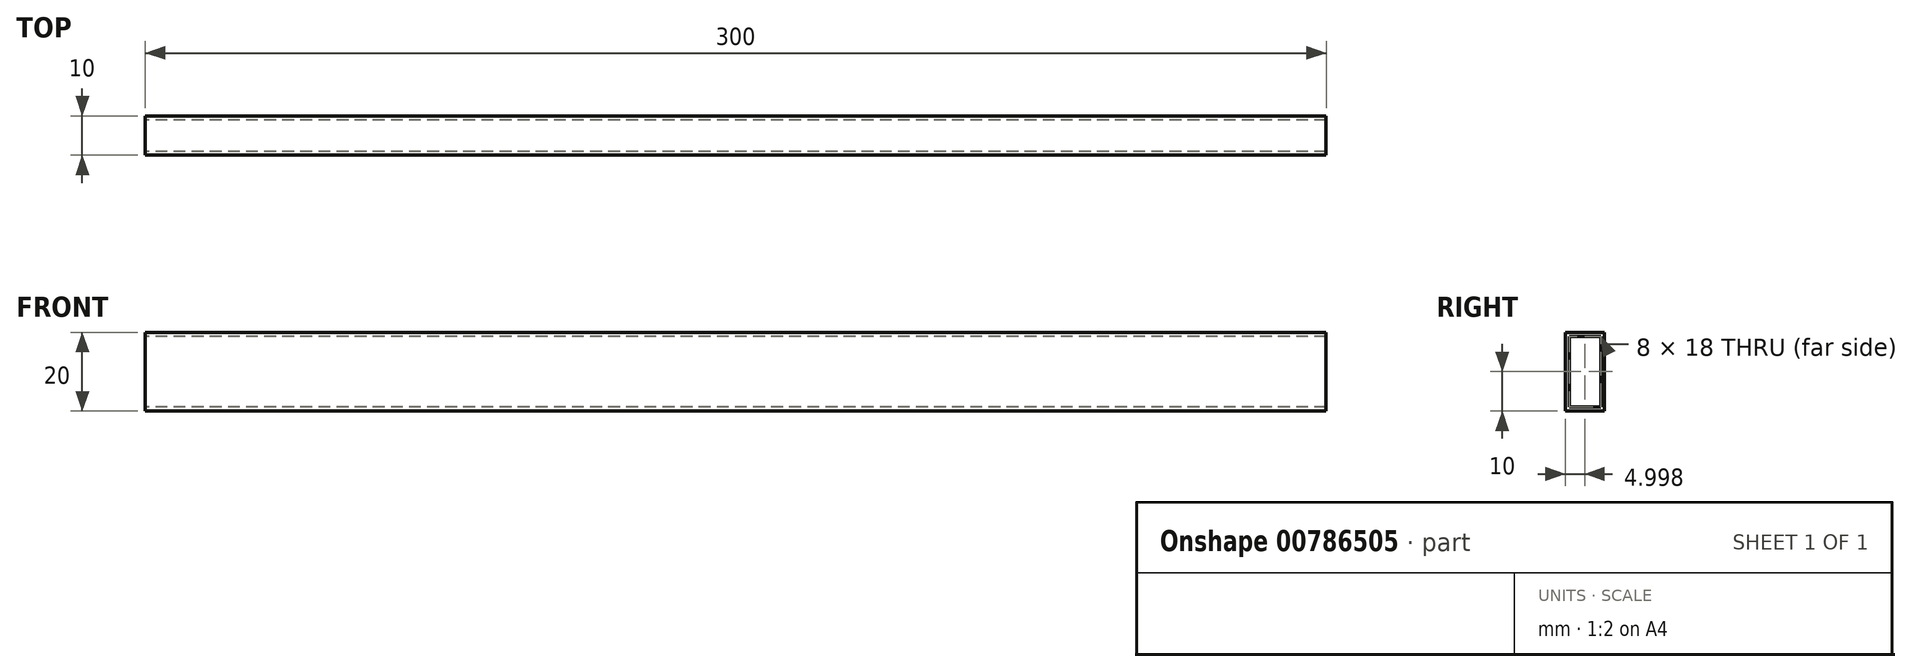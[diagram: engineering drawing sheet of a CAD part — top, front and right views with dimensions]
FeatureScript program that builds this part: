
annotation { "Feature Type Name" : "Feature", "Feature Type Description" : "" }
export const myFeature = defineFeature(function(context is Context, id is Id, definition is map)
    precondition{}
    {
        {
            var Q0;
            Q0=qCreatedBy(makeId("Top.planeOp"),FACE);
            var sketch = newSketch(context, id + "F0", { "sketchPlane" : qUnion([Q0])});
            skLineSegment(sketch, "E0.bottom", {"start": v(24.14, 3.5) * mm, "end": v(324.14, 3.5) * mm});
            skLineSegment(sketch, "E0.top", {"start": v(24.14, -6.5) * mm, "end": v(324.14, -6.5) * mm});
            skLineSegment(sketch, "E0.left", {"start": v(24.14, 3.5) * mm, "end": v(24.14, -6.5) * mm});
            skLineSegment(sketch, "E0.right", {"start": v(324.14, 3.5) * mm, "end": v(324.14, -6.5) * mm});
            skSolve(sketch);
        }
        {
            var Q0;
            Q0=qSketchRegion(id+"F0",true);
            extrude(context, id + "F1", {"entities" : qUnion([Q0]), "depth" : 20 * mm, "offsetDistance" : 25 * mm});
        }
        {
            var Q0;
            Q0=makeQuery(id+"F1.opExtrude","SWEPT_FACE",FACE,{"disambiguationData":[OSD([sQuery(id+"F0.wireOp",EDGE,"E0.left")])]});
            var sketch = newSketch(context, id + "F2", { "sketchPlane" : qUnion([Q0])});
            skLineSegment(sketch, "E1.bottom", {"start": v(-2.5, 1) * mm, "end": v(5.5, 1) * mm});
            skLineSegment(sketch, "E1.top", {"start": v(-2.5, 19) * mm, "end": v(5.5, 19) * mm});
            skLineSegment(sketch, "E1.left", {"start": v(-2.5, 1) * mm, "end": v(-2.5, 19) * mm});
            skLineSegment(sketch, "E1.right", {"start": v(5.5, 1) * mm, "end": v(5.5, 19) * mm});
            skSolve(sketch);
        }
        {
            var Q0;
            Q0=qSketchRegion(id+"F2",true);
            extrude(context, id + "F3", {"entities" : qUnion([Q0]), "operationType" : NewBodyOperationType.REMOVE, "oppositeDirection" : true, "depth" : 300 * mm, "offsetDistance" : 25 * mm});
        }
    });
